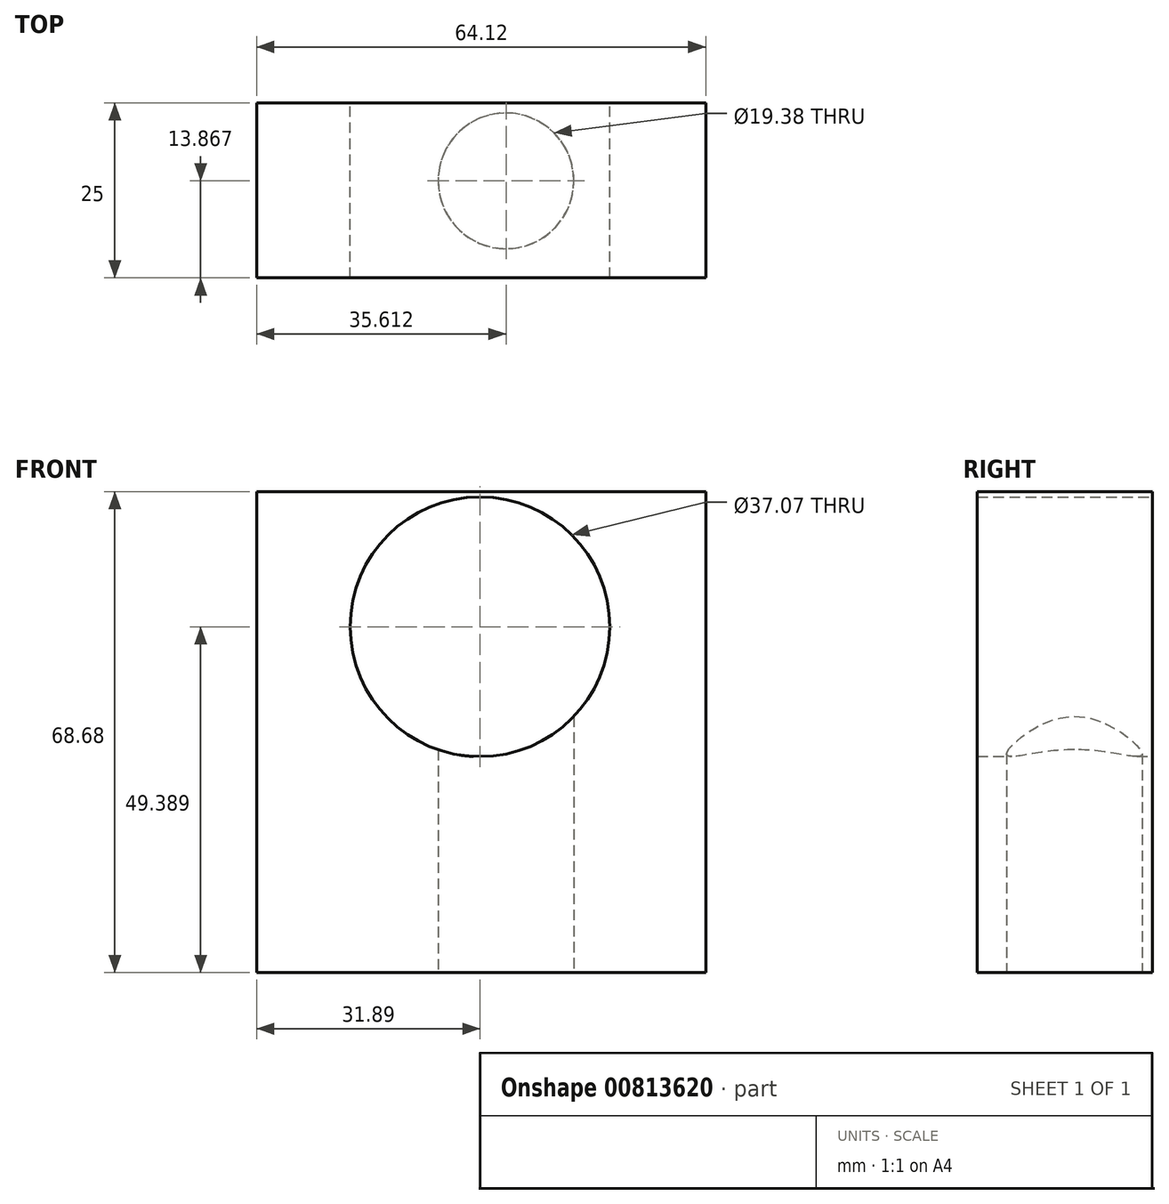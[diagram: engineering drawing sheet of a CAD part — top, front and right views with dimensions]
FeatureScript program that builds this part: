
annotation { "Feature Type Name" : "Feature", "Feature Type Description" : "" }
export const myFeature = defineFeature(function(context is Context, id is Id, definition is map)
    precondition{}
    {
        {
            var Q0;
            Q0=qCreatedBy(makeId("Front.planeOp"),FACE);
            var sketch = newSketch(context, id + "F0", { "sketchPlane" : qUnion([Q0])});
            skLineSegment(sketch, "E0.bottom", {"start": v(-24.58, -26.1) * mm, "end": v(39.54, -26.1) * mm});
            skLineSegment(sketch, "E0.top", {"start": v(-24.58, 42.6) * mm, "end": v(39.54, 42.6) * mm});
            skLineSegment(sketch, "E0.left", {"start": v(-24.58, -26.1) * mm, "end": v(-24.58, 42.6) * mm});
            skLineSegment(sketch, "E0.right", {"start": v(39.54, -26.1) * mm, "end": v(39.54, 42.6) * mm});
            skCircle(sketch, "E1", {"center": v(7.3, 23.3) * mm, "radius": 18.53 * mm});
            skSolve(sketch);
        }
        {
            var Q0;
            Q0 = qSketchRegion(id + "F0", true);
            extrude(context, id + "F1", {"entities" : qUnion([Q0]), "depth" : 25 * mm, "offsetDistance" : 25 * mm});
        }
        {
            var Q0;
            Q0=makeQuery(id+"F1.opExtrude","SWEPT_FACE",FACE,{"disambiguationData":[OSD([sQuery(id+"F0.wireOp",EDGE,"E0.bottom")])]});
            var sketch = newSketch(context, id + "F2", { "sketchPlane" : qUnion([Q0])});
            skCircle(sketch, "E2", {"center": v(11.03, 11.13) * mm, "radius": 9.69 * mm});
            skSolve(sketch);
        }
        {
            var Q0;
            Q0 = qSketchRegion(id + "F2", true);
            extrude(context, id + "F3", {"entities" : qUnion([Q0]), "operationType" : NewBodyOperationType.REMOVE, "oppositeDirection" : true, "depth" : 40 * mm, "offsetDistance" : 25 * mm});
        }
    });
